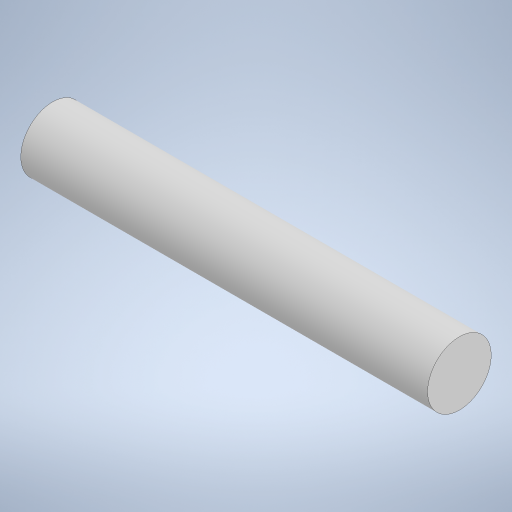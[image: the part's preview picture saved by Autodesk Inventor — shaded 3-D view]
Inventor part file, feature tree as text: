
AUTODESK INVENTOR PART (.ipt)
format: ipt  version: 2023 (Build 270158000, 158)  size: 219,648 bytes
history: native  units: in
note: dims shown in document units (in); Inventor stores cm internally (conversion verified against a paired STEP export)
features: extrude x1, sketch x1
ambient origin geometry x8: Origin, YZ Plane, XZ Plane, XY Plane, X Axis, Y Axis, Z Axis, Center Point
bodies: Solid1 (feature_tree)
feature tree (2):
  extrude  "Extrusion1"  Depth=0.5in TaperAngle=0.0deg
  sketch  "Sketch1"  dims[d0=0.0781in d1=0.5in d2=0.0in]
